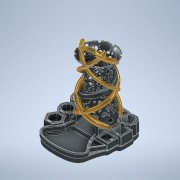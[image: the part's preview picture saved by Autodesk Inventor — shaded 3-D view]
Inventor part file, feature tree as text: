
AUTODESK INVENTOR PART (.ipt)
format: ipt  version: 2022 (Build 260153000, 153)  size: 8,963,072 bytes
history: native  units: mm
features: sketch x29, extrude x25, fillet x12, helix x5, plane x3, chamfer x3, revolve x2, pattern_circular x2
ambient origin geometry x8: Origin, YZ Plane, XZ Plane, XY Plane, X Axis, Y Axis, Z Axis, Center Point
bodies: Solid1 (feature_tree)
feature tree (81):
  revolve  "Revolution1"  [1 undecoded]
  plane  "Work Plane1"
  extrude  "Extrusion4"  Depth=20.0mm
  extrude  "Extrusion2"  Depth=19.0mm
  pattern_circular  "Circular Pattern2"  Count=9  [1 undecoded]
  plane  "Work Plane3"
  extrude  "Extrusion3"  Depth=10.0mm
  pattern_circular  "Circular Pattern3"  Count=7  [1 undecoded]
  helix  "Coil1"  [1 undecoded]
  helix  "Coil2"  [1 undecoded]
  helix  "Coil3"  [1 undecoded]
  helix  "Coil4"  [1 undecoded]
  helix  "Coil5"  [1 undecoded]
  extrude  "Extrusion5"  Depth=20.0mm
  revolve  "Revolution2"  [1 undecoded]
  extrude  "Extrusion6"  Depth=30.0mm
  extrude  "Extrusion7"  Depth=15.0mm
  extrude  "Extrusion15"  Depth=30.0mm
  extrude  "Extrusion16"  Depth=45.0mm
  extrude  "Extrusion17"  Depth=10.0mm
  extrude  "Extrusion18"  Depth=10.0mm
  extrude  "Extrusion19"  Depth=10.0mm
  extrude  "Extrusion20"  Depth=10.0mm
  extrude  "Extrusion21"  Depth=10.0mm
  extrude  "Extrusion22"  Depth=10.0mm
  extrude  "Extrusion23"  Depth=10.0mm TaperAngle=0.0deg
  extrude  "Extrusion25"  Depth=60.0mm
  fillet  "Fillet3"  [1 undecoded]
  extrude  "Extrusion26"  Depth=54.0mm TaperAngle=0.0deg
  extrude  "Extrusion27"  Depth=35.0mm
  extrude  "Extrusion28"  Depth=1.0mm
  extrude  "Extrusion29"  Depth=1.0mm
  extrude  "Extrusion30"  Depth=35.0mm
  extrude  "Extrusion31"  Depth=35.0mm
  extrude  "Extrusion32"  Depth=1.0mm
  chamfer  "Chamfer1"  Distance=10.0mm
  extrude  "Extrusion33"  Depth=1.0mm TaperAngle=0.0deg
  chamfer  "Chamfer2"  Distance=10.0mm
  chamfer  "Chamfer3"  Distance=15.0mm
  fillet  "Fillet4"  Radius=0.2mm
  fillet  "Fillet5"  Radius=5.0mm
  fillet  "Fillet6"  Radius=10.0mm
  fillet  "Fillet8"  Radius=15.0mm
  fillet  "Fillet9"  Radius=10.0mm
  fillet  "Fillet10"  Radius=7.0mm
  fillet  "Fillet11"  Radius=3.6mm
  fillet  "Fillet12"  Radius=10.0mm
  fillet  "Fillet13"  Radius=20.0mm
  fillet  "Fillet14"  Radius=24.0mm
  extrude  "Extrusion34"  Depth=1.0mm
  fillet  "Fillet15"  Radius=30.0mm
  sketch  "Sketch1"  dims[d11=60.0mm d12=40.0mm]
  sketch  "Sketch3"  dims[d13=20.0mm d14=20.0mm]
  plane  "Work Plane2"
  sketch  "Sketch4"  dims[d15=20.0mm d16=19.0mm d17=90.0mm]
  sketch  "Sketch5"  dims[d18=30.0mm d19=10.0mm]
  sketch  "Sketch7"  dims[d20=149.0mm]
  sketch  "Sketch8"  dims[d26=2.0mm]
  sketch  "Sketch9"  dims[d27=2.0mm]
  sketch  "Sketch10"  dims[d28=2.0mm]
  sketch  "Sketch11"  dims[d29=2.0mm]
  sketch  "Sketch13"  dims[d30=2.0mm]
  sketch  "Sketch16"  dims[d31=90.0deg d32=70.0mm d38=77.75mm d39=0.0mm d40=40.0mm d41=360.0deg d43=70.0mm d44=77.75mm d45=0.0mm d46=40.0mm d47=360.0deg]
  sketch  "Sketch17"  dims[d49=20.0mm d50=20.0mm]
  sketch  "Sketch20"  dims[d51=20.0mm d52=20.0mm]
  sketch  "Sketch21"  dims[d53=40.0mm d54=30.0mm]
  sketch  "Sketch22"  dims[d55=30.0mm d56=15.0mm]
  sketch  "Sketch23"  dims[d57=15.0mm d58=30.0mm]
  sketch  "Sketch26"  dims[d59=77.75mm d60=0.0mm d61=45.0mm]
  sketch  "Sketch27"  dims[d62=35.0mm]
  sketch  "Sketch28"  dims[d63=70.0mm d64=100.0mm d65=10.0mm d66=-0.567232mm d67=90.0deg d68=90.0deg d69=90.0deg d70=90.0deg d71=13.0mm]
  sketch  "Sketch30"  dims[d72=10.0mm d73=39.0mm]
  sketch  "Sketch31"  dims[d74=140.0mm d75=160.0mm d76=10.0mm d77=-0.645772mm d78=90.0deg d79=90.0deg d80=90.0deg d81=90.0deg d82=11.0mm]
  sketch  "Sketch33"  dims[d83=39.0mm d84=10.0mm]
  sketch  "Sketch35"  dims[d85=135.0mm d86=160.0mm d87=10.0mm d88=-0.645772mm d89=90.0deg d90=90.0deg d91=90.0deg d92=90.0deg d93=11.0mm]
  sketch  "Sketch37"  dims[d94=170.0mm d95=160.0mm d96=10.0mm d97=-0.645772mm d98=90.0deg d99=90.0deg d100=90.0deg d101=90.0deg d102=9.0mm]
  sketch  "Sketch38"  dims[d103=170.0mm d104=160.0mm d105=10.0mm d106=-0.645772mm d107=90.0deg d108=90.0deg d109=90.0deg d110=90.0deg d125=3.0mm d126=0.0mm]
  sketch  "Sketch39"  dims[d128=60.0mm d129=43.0mm d130=270.0deg]
  sketch  "Sketch40"  dims[d132=34.0mm d133=54.0mm d134=0.0mm]
  sketch  "Sketch41"  dims[d136=54.0mm d137=0.0mm d141=35.0mm]
  sketch  "Sketch43"  dims[d165=35.0mm d166=30.0mm d167=30.0mm d168=30.0mm d169=30.0mm d170=35.0mm d172=35.0mm d186=5.0mm d187=10.0mm d188=0.0mm d190=5.0mm d191=0.0mm d192=10.0mm d193=0.0mm d194=15.0mm d195=0.0mm d196=0.2mm d197=0.0mm d198=5.0mm d199=0.0mm d200=10.0mm d201=0.0mm d202=15.0mm d203=0.0mm d204=10.0mm d205=0.0mm d210=7.0mm d211=0.0mm d212=3.6mm d213=10.0mm d214=0.0mm d215=20.0mm d216=24.0mm d217=20.0mm d218=30.0mm d219=23.5mm d220=5.75mm d221=5.75mm d222=5.75mm d223=14.0mm d224=0.0mm d225=22.5mm d226=6.25mm d227=6.25mm d228=6.25mm d229=14.0mm d230=0.0mm d231=25.0mm d232=5.0mm d233=5.0mm d234=5.0mm d235=14.0mm d236=0.0mm d237=25.5mm d239=3.0mm d241=10.0mm d242=0.0mm d243=54.0mm d244=43.0mm d245=17.5mm d246=17.5mm d247=7.0mm d248=5.5mm d249=4.0mm d250=3.607976mm d251=10.0mm d252=0.0mm d253=21.0mm d254=21.0mm d255=5.0mm d256=4.0mm d257=5.0mm d258=24.0mm d259=0.0mm d260=10.0mm d261=2.0mm d262=45.0deg d263=25.0mm d266=5.0mm d267=5.0mm d268=12.0mm d269=0.0mm d270=11.0mm d271=2.0mm d272=45.0deg d273=12.0mm d274=2.0mm d275=45.0deg d276=35.0mm d277=3.0mm d278=5.0mm d279=5.0mm d280=5.0mm d281=2.0mm d282=2.0mm d283=1.56mm d285=1.0mm d286=1.0mm d287=1.0mm d288=1.0mm d289=1.0mm d290=1.0mm d291=1.0mm d292=20.0mm d293=0.0mm d294=1.0mm d135=0.0mm]
note: 10 required parameter values undecoded (feature->parameter linkage not recoverable at this tier; creation-order binding heuristic only, values carry confidence <= 0.55)